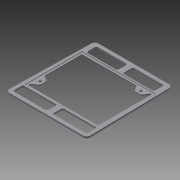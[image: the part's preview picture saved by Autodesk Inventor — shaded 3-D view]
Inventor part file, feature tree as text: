
AUTODESK INVENTOR PART (.ipt)
format: ipt  version: 2014 SP1 (Build 180222100, 222)  size: 223,744 bytes
history: native  units: in
note: dims shown in document units (in); Inventor stores cm internally (conversion verified against a paired STEP export)
features: extrude x5, sketch x4, fillet x2
ambient origin geometry x8: Origin, YZ Plane, XZ Plane, XY Plane, X Axis, Y Axis, Z Axis, Center Point
bodies: Solid1 (feature_tree)
feature tree (11):
  extrude  "Extrusion1"  Depth=0.25in
  fillet  "Fillet1"  Radius=0.25in
  fillet  "Fillet4"  Radius=6.375in
  extrude  "Extrusion20"  Depth=5.9in
  extrude  "Extrusion22"  Depth=0.12in TaperAngle=0.0deg
  extrude  "Extrusion23"  Depth=0.75in
  extrude  "Extrusion29"  Depth=2.5in
  sketch  "Sketch21"  dims[d2=0.12in d3=0.0in d4=0.25in d71=0.25in d74=6.375in]
  sketch  "Sketch23"  dims[d75=5.65in d76=5.9in]
  sketch  "Sketch25"  dims[d97=0.125in d98=0.12in d99=0.0in]
  sketch  "Sketch34"  dims[d111=0.75in d112=0.75in d113=2.5in d114=2.5in d129=5.35in d130=4.18in d131=0.3901in d132=0.125in d133=0.125in d134=0.125in d135=0.125in d136=0.12in d137=0.0in d138=0.125in d139=0.05in d140=0.0in d141=0.75in d142=0.125in d223=0.125in d226=0.19in d227=0.81in d228=0.3125in d231=0.5in d235=0.125in d236=0.07in d237=0.0in d240=0.19in d241=0.735in d242=0.3125in d244=0.5in d247=0.125in d248=0.32in d249=0.32in d250=0.18in d251=0.18in d253=0.22in d254=0.18in d255=0.18in]
